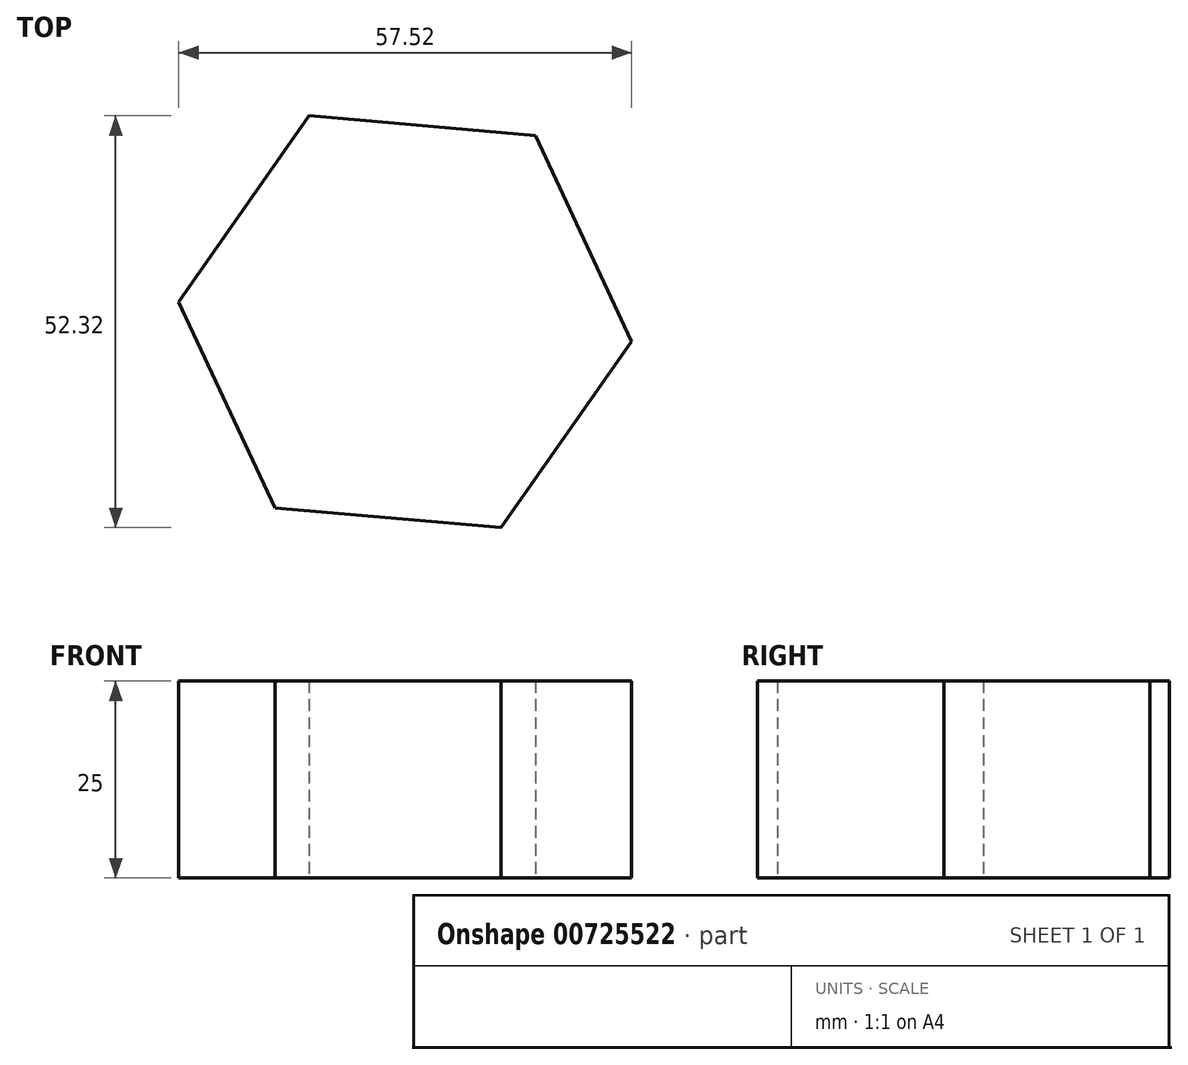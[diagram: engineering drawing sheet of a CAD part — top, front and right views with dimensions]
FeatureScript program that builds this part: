
annotation { "Feature Type Name" : "Feature", "Feature Type Description" : "" }
export const myFeature = defineFeature(function(context is Context, id is Id, definition is map)
    precondition{}
    {
        {
            var Q0;
            Q0=qCreatedBy(makeId("Top.planeOp"),FACE);
            var sketch = newSketch(context, id + "F0", { "sketchPlane" : qUnion([Q0])});
            skCircle(sketch, "E0.cCircle", {"center": v(0, 0) * mm, "radius": 25 * mm, "construction": true});
            skLineSegment(sketch, "E0.0", {"start": v(-12.2, 26.16) * mm, "end": v(16.56, 23.65) * mm});
            skLineSegment(sketch, "E0.1", {"start": v(16.56, 23.65) * mm, "end": v(28.76, -2.52) * mm});
            skLineSegment(sketch, "E0.2", {"start": v(28.76, -2.52) * mm, "end": v(12.2, -26.16) * mm});
            skLineSegment(sketch, "E0.3", {"start": v(12.2, -26.16) * mm, "end": v(-16.56, -23.65) * mm});
            skLineSegment(sketch, "E0.4", {"start": v(-16.56, -23.65) * mm, "end": v(-28.76, 2.52) * mm});
            skLineSegment(sketch, "E0.5", {"start": v(-28.76, 2.52) * mm, "end": v(-12.2, 26.16) * mm});
            skPoint(sketch, "E0.0.midPoint", {"position": v(2.18, 24.9) * mm});
            skLineSegment(sketch, "E1", {"start": v(0, 0) * mm, "end": v(-20.48, 14.34) * mm});
            skLineSegment(sketch, "E2", {"start": v(0, 0) * mm, "end": v(-17.68, 17.68) * mm});
            skLineSegment(sketch, "E3", {"start": v(-17.68, 17.68) * mm, "end": v(-56.8, 17.68) * mm});
            skPoint(sketch, "E4", {"position": v(-18.14, 17.68) * mm});
            skLineSegment(sketch, "E5", {"start": v(-18.14, 17.68) * mm, "end": v(-28.2, 24.72) * mm});
            skLineSegment(sketch, "E6.MirrorCS", {"start": v(-17.98, 17.24) * mm, "end": v(-31.36, 54) * mm});
            skSolve(sketch);
        }
        {
            var Q0;
            {var subQ0=sQuery(id+"F0.wireOp",EDGE,"E1");Q0=makeQuery(id+"F0.imprint","IMPRINT",FACE,{"disambiguationData":[TD([[makeQuery(id+"F0.imprint","IMPRINT",EDGE,{"derivedFrom":subQ0}),-1.0]])]});}
            var Q1;
            {var subQ0=sQuery(id+"F0.wireOp",EDGE,"E0.0");Q1=makeQuery(id+"F0.imprint","IMPRINT",FACE,{"disambiguationData":[TD([[makeQuery(id+"F0.imprint","IMPRINT",EDGE,{"derivedFrom":subQ0}),-1.0]])]});}
            extrude(context, id + "F1", {"entities" : qUnion([Q0, Q1]), "depth" : 25 * mm, "offsetDistance" : 25 * mm});
        }
    });
